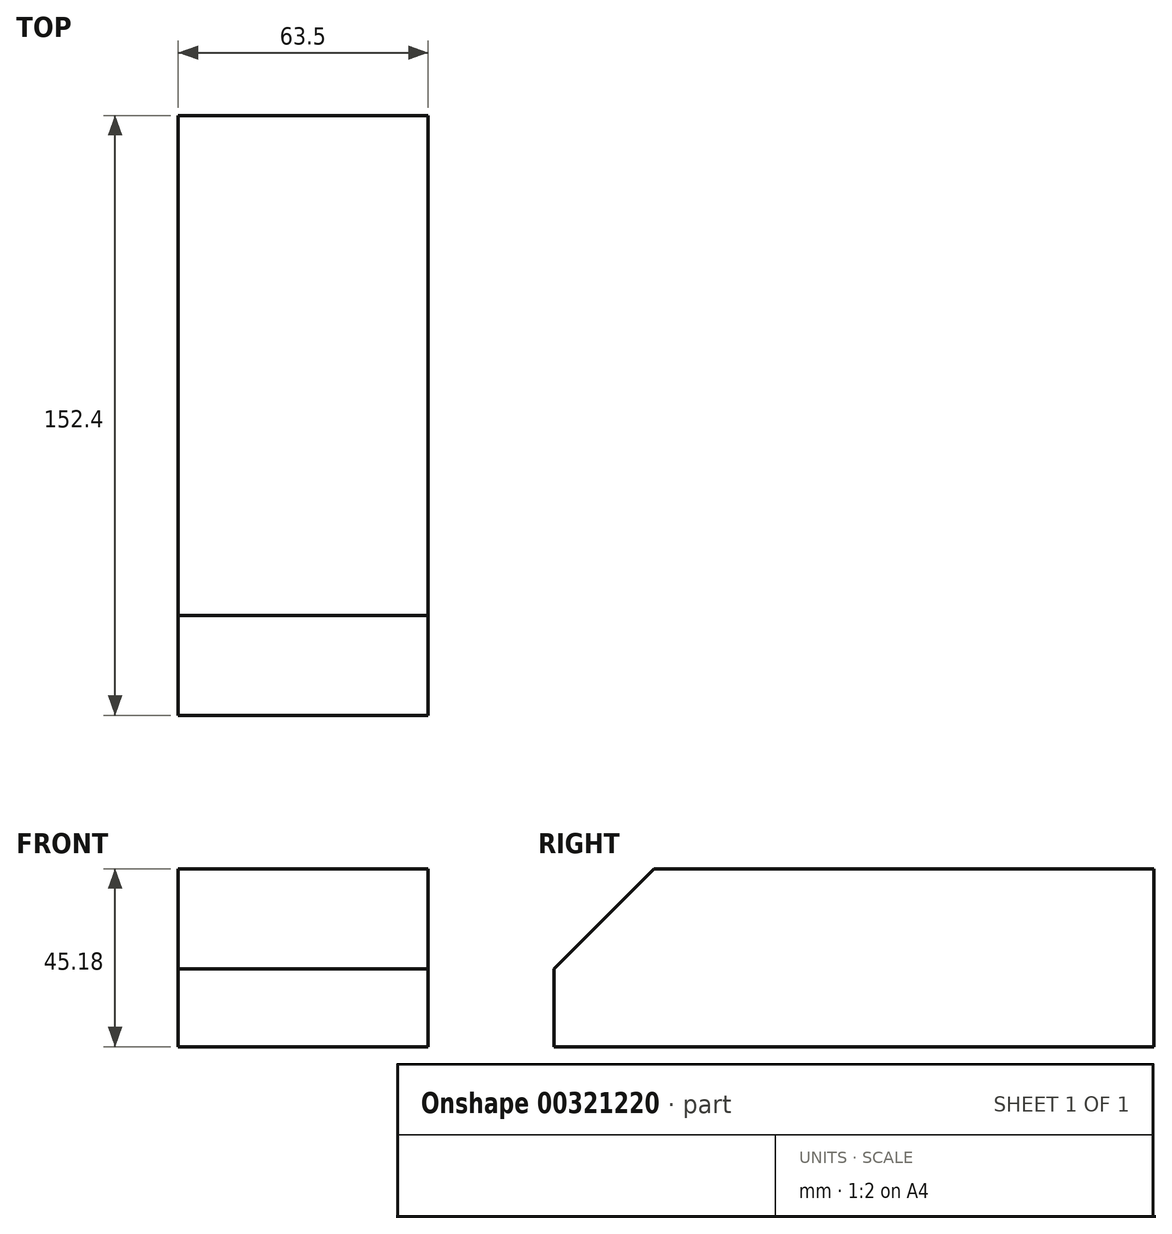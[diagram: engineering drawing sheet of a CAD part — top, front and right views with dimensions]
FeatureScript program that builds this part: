
annotation { "Feature Type Name" : "Feature", "Feature Type Description" : "" }
export const myFeature = defineFeature(function(context is Context, id is Id, definition is map)
    precondition{}
    {
        {
            var Q0;
            Q0=qCreatedBy(makeId("Right.planeOp"),FACE);
            var sketch = newSketch(context, id + "F0", { "sketchPlane" : qUnion([Q0])});
            skLineSegment(sketch, "E0.bottom", {"start": v(76.2, -22.6) * mm, "end": v(-76.2, -22.6) * mm});
            skLineSegment(sketch, "E0.top", {"start": v(76.2, 22.6) * mm, "end": v(-76.2, 22.6) * mm});
            skLineSegment(sketch, "E0.left", {"start": v(76.2, -22.6) * mm, "end": v(76.2, 22.6) * mm});
            skLineSegment(sketch, "E0.right", {"start": v(-76.2, -22.6) * mm, "end": v(-76.2, 22.6) * mm});
            skPoint(sketch, "E0.middle", {"position": v(0, 0) * mm});
            skSolve(sketch);
        }
        {
            var Q0;
            Q0 = qSketchRegion(id + "F0", true);
            extrude(context, id + "F1", {"entities" : qUnion([Q0]), "oppositeDirection" : true, "depth" : 63.5 * mm});
        }
        {
            var Q0;
            Q0=makeQuery(id+"F1.opExtrude","SWEPT_EDGE",EDGE,{"disambiguationData":[OSD([sQuery(id+"F0.wireOp",EDGE,"E0.top"),sQuery(id+"F0.wireOp",EDGE,"E0.right")])]});
            chamfer(context, id + "F2", {"entities" : qUnion([Q0]), "width" : 25.4 * mm, "tangentPropagation" : true});
        }
    });
